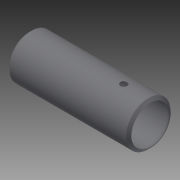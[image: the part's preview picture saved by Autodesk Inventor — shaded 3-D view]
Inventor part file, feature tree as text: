
AUTODESK INVENTOR PART (.ipt)
format: ipt  version: 2014 (Build 180170000, 170)  size: 137,728 bytes
history: native  units: in
note: dims shown in document units (in); Inventor stores cm internally (conversion verified against a paired STEP export)
features: other x56, revolve x2, sketch x2
ambient origin geometry x8: Origin, YZ Plane, XZ Plane, XY Plane, X Axis, Y Axis, Z Axis, Center Point
bodies: Solid1 (feature_tree)
feature tree (60):
  revolve  "Revolution1"  Angle=360.0deg
  revolve  "Revolution2"  [1 undecoded]
  other  "o1_XY"
  other  "o1_YZ"
  other  "o1_ZX"
  other  "o1_X"
  other  "o1_Y"
  other  "o1_Z"
  other  "o1_Center"
  other  "o2_XY"
  other  "o2_YZ"
  other  "o2_ZX"
  other  "o2_X"
  other  "o2_Y"
  other  "o2_Z"
  other  "o2_Center"
  other  "t1_XY"
  other  "t1_YZ"
  other  "t1_ZX"
  other  "t1_X"
  other  "t1_Y"
  other  "t1_Z"
  other  "t1_Center"
  other  "t2_XY"
  other  "t2_YZ"
  other  "t2_ZX"
  other  "t2_X"
  other  "t2_Y"
  other  "t2_Z"
  other  "t2_Center"
  other  "t3_XY"
  other  "t3_YZ"
  other  "t3_ZX"
  other  "t3_X"
  other  "t3_Y"
  other  "t3_Z"
  other  "t3_Center"
  other  "t4_XY"
  other  "t4_YZ"
  other  "t4_ZX"
  other  "t4_X"
  other  "t4_Y"
  other  "t4_Z"
  other  "t4_Center"
  other  "tube1_XY"
  other  "tube1_YZ"
  other  "tube1_ZX"
  other  "tube1_X"
  other  "tube1_Y"
  other  "tube1_Z"
  other  "tube1_Center"
  other  "tube2_XY"
  other  "tube2_YZ"
  other  "tube2_ZX"
  other  "tube2_X"
  other  "tube2_Y"
  other  "tube2_Z"
  other  "tube2_Center"
  sketch  "Sketch_5"
  sketch  "Sketch_1"  dims[d0=360.0deg d1=360.0deg]
note: 1 required parameter value undecoded (feature->parameter linkage not recoverable at this tier; creation-order binding heuristic only, values carry confidence <= 0.55)
